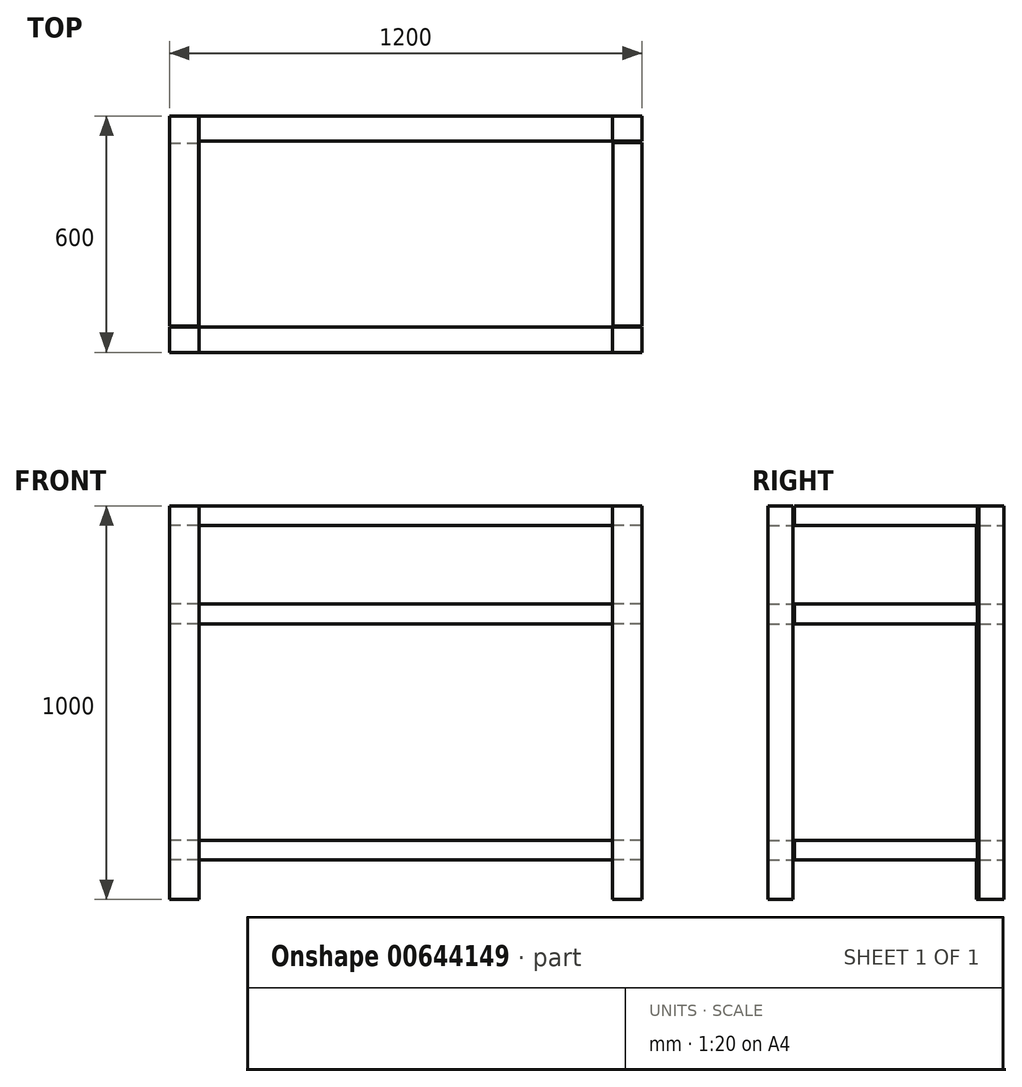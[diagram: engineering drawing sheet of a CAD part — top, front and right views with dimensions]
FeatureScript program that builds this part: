
annotation { "Feature Type Name" : "Feature", "Feature Type Description" : "" }
export const myFeature = defineFeature(function(context is Context, id is Id, definition is map)
    precondition{}
    {
        {
            var Q0;
            Q0=qCreatedBy(makeId("Top.planeOp"),FACE);
            var sketch = newSketch(context, id + "F0", { "sketchPlane" : qUnion([Q0])});
            skLineSegment(sketch, "E0.bottom", {"start": v(-600, 300) * mm, "end": v(-526, 300) * mm});
            skLineSegment(sketch, "E0.top", {"start": v(-600, 230) * mm, "end": v(-526, 230) * mm});
            skLineSegment(sketch, "E0.left", {"start": v(-600, 300) * mm, "end": v(-600, 230) * mm});
            skLineSegment(sketch, "E0.right", {"start": v(-526, 300) * mm, "end": v(-526, 230) * mm});
            skLineSegment(sketch, "E1.bottom", {"start": v(525, 300) * mm, "end": v(600, 300) * mm});
            skLineSegment(sketch, "E1.top", {"start": v(525, 236) * mm, "end": v(600, 236) * mm});
            skLineSegment(sketch, "E1.left", {"start": v(525, 300) * mm, "end": v(525, 236) * mm});
            skLineSegment(sketch, "E1.right", {"start": v(600, 300) * mm, "end": v(600, 236) * mm});
            skLineSegment(sketch, "E2.bottom", {"start": v(600, -236) * mm, "end": v(525, -236) * mm});
            skLineSegment(sketch, "E2.top", {"start": v(600, -300) * mm, "end": v(525, -300) * mm});
            skLineSegment(sketch, "E2.left", {"start": v(600, -236) * mm, "end": v(600, -300) * mm});
            skLineSegment(sketch, "E2.right", {"start": v(525, -236) * mm, "end": v(525, -300) * mm});
            skLineSegment(sketch, "E3.bottom", {"start": v(-525, -236) * mm, "end": v(-600, -236) * mm});
            skLineSegment(sketch, "E3.top", {"start": v(-525, -300) * mm, "end": v(-600, -300) * mm});
            skLineSegment(sketch, "E3.left", {"start": v(-525, -236) * mm, "end": v(-525, -300) * mm});
            skLineSegment(sketch, "E3.right", {"start": v(-600, -236) * mm, "end": v(-600, -300) * mm});
            skSolve(sketch);
        }
        {
            var Q0;
            Q0=makeQuery(id+"F0.imprint","IMPRINT",FACE,{"disambiguationData":[TD([[makeQuery(id+"F0.imprint","IMPRINT",EDGE,{"derivedFrom":sQuery(id+"F0.wireOp",EDGE,"E0.bottom")}),-1.0]])]});
            var Q1;
            Q1=makeQuery(id+"F0.imprint","IMPRINT",FACE,{"disambiguationData":[TD([[makeQuery(id+"F0.imprint","IMPRINT",EDGE,{"derivedFrom":sQuery(id+"F0.wireOp",EDGE,"E3.bottom")}),1.0]])]});
            var Q2;
            Q2=makeQuery(id+"F0.imprint","IMPRINT",FACE,{"disambiguationData":[TD([[makeQuery(id+"F0.imprint","IMPRINT",EDGE,{"derivedFrom":sQuery(id+"F0.wireOp",EDGE,"E2.bottom")}),1.0]])]});
            var Q3;
            Q3=makeQuery(id+"F0.imprint","IMPRINT",FACE,{"disambiguationData":[TD([[makeQuery(id+"F0.imprint","IMPRINT",EDGE,{"derivedFrom":sQuery(id+"F0.wireOp",EDGE,"E1.bottom")}),-1.0]])]});
            extrude(context, id + "F1", {"entities" : qUnion([Q0, Q1, Q2, Q3]), "depth" : 1000 * mm, "offsetDistance" : 25 * mm});
        }
        {
            var Q0;
            Q0=qCreatedBy(makeId("Right.planeOp"),FACE);
            var sketch = newSketch(context, id + "F2", { "sketchPlane" : qUnion([Q0])});
            skLineSegment(sketch, "E4.bottom", {"start": v(-300, 150) * mm, "end": v(-236, 150) * mm});
            skLineSegment(sketch, "E4.top", {"start": v(-300, 100) * mm, "end": v(-236, 100) * mm});
            skLineSegment(sketch, "E4.left", {"start": v(-300, 150) * mm, "end": v(-300, 100) * mm});
            skLineSegment(sketch, "E4.right", {"start": v(-236, 150) * mm, "end": v(-236, 100) * mm});
            skLineSegment(sketch, "E5.bottom", {"start": v(236, 150) * mm, "end": v(300, 150) * mm});
            skLineSegment(sketch, "E5.top", {"start": v(236, 100) * mm, "end": v(300, 100) * mm});
            skLineSegment(sketch, "E5.left", {"start": v(236, 150) * mm, "end": v(236, 100) * mm});
            skLineSegment(sketch, "E5.right", {"start": v(300, 150) * mm, "end": v(300, 100) * mm});
            skLineSegment(sketch, "E6.bottom", {"start": v(-300, 1000) * mm, "end": v(-236, 1000) * mm});
            skLineSegment(sketch, "E6.top", {"start": v(-300, 950) * mm, "end": v(-236, 950) * mm});
            skLineSegment(sketch, "E6.left", {"start": v(-300, 1000) * mm, "end": v(-300, 950) * mm});
            skLineSegment(sketch, "E6.right", {"start": v(-236, 1000) * mm, "end": v(-236, 950) * mm});
            skLineSegment(sketch, "E7.bottom", {"start": v(236, 1000) * mm, "end": v(300, 1000) * mm});
            skLineSegment(sketch, "E7.top", {"start": v(236, 950) * mm, "end": v(300, 950) * mm});
            skLineSegment(sketch, "E7.left", {"start": v(236, 1000) * mm, "end": v(236, 950) * mm});
            skLineSegment(sketch, "E7.right", {"start": v(300, 1000) * mm, "end": v(300, 950) * mm});
            skLineSegment(sketch, "E8.bottom", {"start": v(-300, 750) * mm, "end": v(-236, 750) * mm});
            skLineSegment(sketch, "E8.top", {"start": v(-300, 700) * mm, "end": v(-236, 700) * mm});
            skLineSegment(sketch, "E8.left", {"start": v(-300, 750) * mm, "end": v(-300, 700) * mm});
            skLineSegment(sketch, "E8.right", {"start": v(-236, 750) * mm, "end": v(-236, 700) * mm});
            skLineSegment(sketch, "E9.bottom", {"start": v(236, 750) * mm, "end": v(300, 750) * mm});
            skLineSegment(sketch, "E9.top", {"start": v(236, 700) * mm, "end": v(300, 700) * mm});
            skLineSegment(sketch, "E9.left", {"start": v(236, 750) * mm, "end": v(236, 700) * mm});
            skLineSegment(sketch, "E9.right", {"start": v(300, 750) * mm, "end": v(300, 700) * mm});
            skSolve(sketch);
        }
        {
            var Q0;
            Q0=makeQuery(id+"F2.imprint","IMPRINT",FACE,{"disambiguationData":[TD([[makeQuery(id+"F2.imprint","IMPRINT",EDGE,{"derivedFrom":sQuery(id+"F2.wireOp",EDGE,"E6.bottom")}),-1.0]])]});
            var Q1;
            Q1=makeQuery(id+"F2.imprint","IMPRINT",FACE,{"disambiguationData":[TD([[makeQuery(id+"F2.imprint","IMPRINT",EDGE,{"derivedFrom":sQuery(id+"F2.wireOp",EDGE,"E8.bottom")}),-1.0]])]});
            var Q2;
            Q2=makeQuery(id+"F2.imprint","IMPRINT",FACE,{"disambiguationData":[TD([[makeQuery(id+"F2.imprint","IMPRINT",EDGE,{"derivedFrom":sQuery(id+"F2.wireOp",EDGE,"E4.bottom")}),-1.0]])]});
            var Q3;
            Q3=makeQuery(id+"F2.imprint","IMPRINT",FACE,{"disambiguationData":[TD([[makeQuery(id+"F2.imprint","IMPRINT",EDGE,{"derivedFrom":sQuery(id+"F2.wireOp",EDGE,"E5.bottom")}),-1.0]])]});
            var Q4;
            Q4=makeQuery(id+"F2.imprint","IMPRINT",FACE,{"disambiguationData":[TD([[makeQuery(id+"F2.imprint","IMPRINT",EDGE,{"derivedFrom":sQuery(id+"F2.wireOp",EDGE,"E9.bottom")}),-1.0]])]});
            var Q5;
            Q5=makeQuery(id+"F2.imprint","IMPRINT",FACE,{"disambiguationData":[TD([[makeQuery(id+"F2.imprint","IMPRINT",EDGE,{"derivedFrom":sQuery(id+"F2.wireOp",EDGE,"E7.bottom")}),-1.0]])]});
            extrude(context, id + "F3", {"entities" : qUnion([Q0, Q1, Q2, Q3, Q4, Q5]), "endBound" : BoundingType.SYMMETRIC, "depth" : 1050 * mm, "offsetDistance" : 25 * mm});
        }
        {
            var Q0;
            Q0=qCreatedBy(makeId("Front.planeOp"),FACE);
            var sketch = newSketch(context, id + "F4", { "sketchPlane" : qUnion([Q0])});
            skLineSegment(sketch, "E10.bottom", {"start": v(600, 150) * mm, "end": v(526, 150) * mm});
            skLineSegment(sketch, "E10.top", {"start": v(600, 100) * mm, "end": v(526, 100) * mm});
            skLineSegment(sketch, "E10.left", {"start": v(600, 150) * mm, "end": v(600, 100) * mm});
            skLineSegment(sketch, "E10.right", {"start": v(526, 150) * mm, "end": v(526, 100) * mm});
            skLineSegment(sketch, "E11.bottom", {"start": v(600, 1000) * mm, "end": v(526, 1000) * mm});
            skLineSegment(sketch, "E11.top", {"start": v(600, 950) * mm, "end": v(526, 950) * mm});
            skLineSegment(sketch, "E11.left", {"start": v(600, 1000) * mm, "end": v(600, 950) * mm});
            skLineSegment(sketch, "E11.right", {"start": v(526, 1000) * mm, "end": v(526, 950) * mm});
            skLineSegment(sketch, "E12.bottom", {"start": v(600, 750) * mm, "end": v(526, 750) * mm});
            skLineSegment(sketch, "E12.top", {"start": v(600, 700) * mm, "end": v(526, 700) * mm});
            skLineSegment(sketch, "E12.left", {"start": v(600, 750) * mm, "end": v(600, 700) * mm});
            skLineSegment(sketch, "E12.right", {"start": v(526, 750) * mm, "end": v(526, 700) * mm});
            skLineSegment(sketch, "E13.bottom", {"start": v(-526, 1000) * mm, "end": v(-600, 1000) * mm});
            skLineSegment(sketch, "E13.top", {"start": v(-526, 950) * mm, "end": v(-600, 950) * mm});
            skLineSegment(sketch, "E13.left", {"start": v(-526, 1000) * mm, "end": v(-526, 950) * mm});
            skLineSegment(sketch, "E13.right", {"start": v(-600, 1000) * mm, "end": v(-600, 950) * mm});
            skLineSegment(sketch, "E14.bottom", {"start": v(-525, 750) * mm, "end": v(-599, 750) * mm});
            skLineSegment(sketch, "E14.top", {"start": v(-525, 700) * mm, "end": v(-599, 700) * mm});
            skLineSegment(sketch, "E14.left", {"start": v(-525, 750) * mm, "end": v(-525, 700) * mm});
            skLineSegment(sketch, "E14.right", {"start": v(-599, 750) * mm, "end": v(-599, 700) * mm});
            skLineSegment(sketch, "E15.bottom", {"start": v(-525, 150) * mm, "end": v(-599, 150) * mm});
            skLineSegment(sketch, "E15.top", {"start": v(-525, 100) * mm, "end": v(-599, 100) * mm});
            skLineSegment(sketch, "E15.left", {"start": v(-525, 150) * mm, "end": v(-525, 100) * mm});
            skLineSegment(sketch, "E15.right", {"start": v(-599, 150) * mm, "end": v(-599, 100) * mm});
            skSolve(sketch);
        }
        {
            var Q0;
            Q0=makeQuery(id+"F4.imprint","IMPRINT",FACE,{"disambiguationData":[TD([[makeQuery(id+"F4.imprint","IMPRINT",EDGE,{"derivedFrom":sQuery(id+"F4.wireOp",EDGE,"E12.bottom")}),1.0]])]});
            var Q1;
            Q1=makeQuery(id+"F4.imprint","IMPRINT",FACE,{"disambiguationData":[TD([[makeQuery(id+"F4.imprint","IMPRINT",EDGE,{"derivedFrom":sQuery(id+"F4.wireOp",EDGE,"E10.bottom")}),1.0]])]});
            var Q2;
            Q2=makeQuery(id+"F4.imprint","IMPRINT",FACE,{"disambiguationData":[TD([[makeQuery(id+"F4.imprint","IMPRINT",EDGE,{"derivedFrom":sQuery(id+"F4.wireOp",EDGE,"E11.bottom")}),1.0]])]});
            var Q3;
            Q3=makeQuery(id+"F4.imprint","IMPRINT",FACE,{"disambiguationData":[TD([[makeQuery(id+"F4.imprint","IMPRINT",EDGE,{"derivedFrom":sQuery(id+"F4.wireOp",EDGE,"E15.bottom")}),1.0]])]});
            var Q4;
            Q4=makeQuery(id+"F4.imprint","IMPRINT",FACE,{"disambiguationData":[TD([[makeQuery(id+"F4.imprint","IMPRINT",EDGE,{"derivedFrom":sQuery(id+"F4.wireOp",EDGE,"E14.bottom")}),1.0]])]});
            var Q5;
            Q5=makeQuery(id+"F4.imprint","IMPRINT",FACE,{"disambiguationData":[TD([[makeQuery(id+"F4.imprint","IMPRINT",EDGE,{"derivedFrom":sQuery(id+"F4.wireOp",EDGE,"E13.bottom")}),1.0]])]});
            extrude(context, id + "F5", {"entities" : qUnion([Q0, Q1, Q2, Q3, Q4, Q5]), "operationType" : NewBodyOperationType.ADD, "endBound" : BoundingType.SYMMETRIC, "depth" : 466 * mm, "offsetDistance" : 25 * mm});
        }
    });
